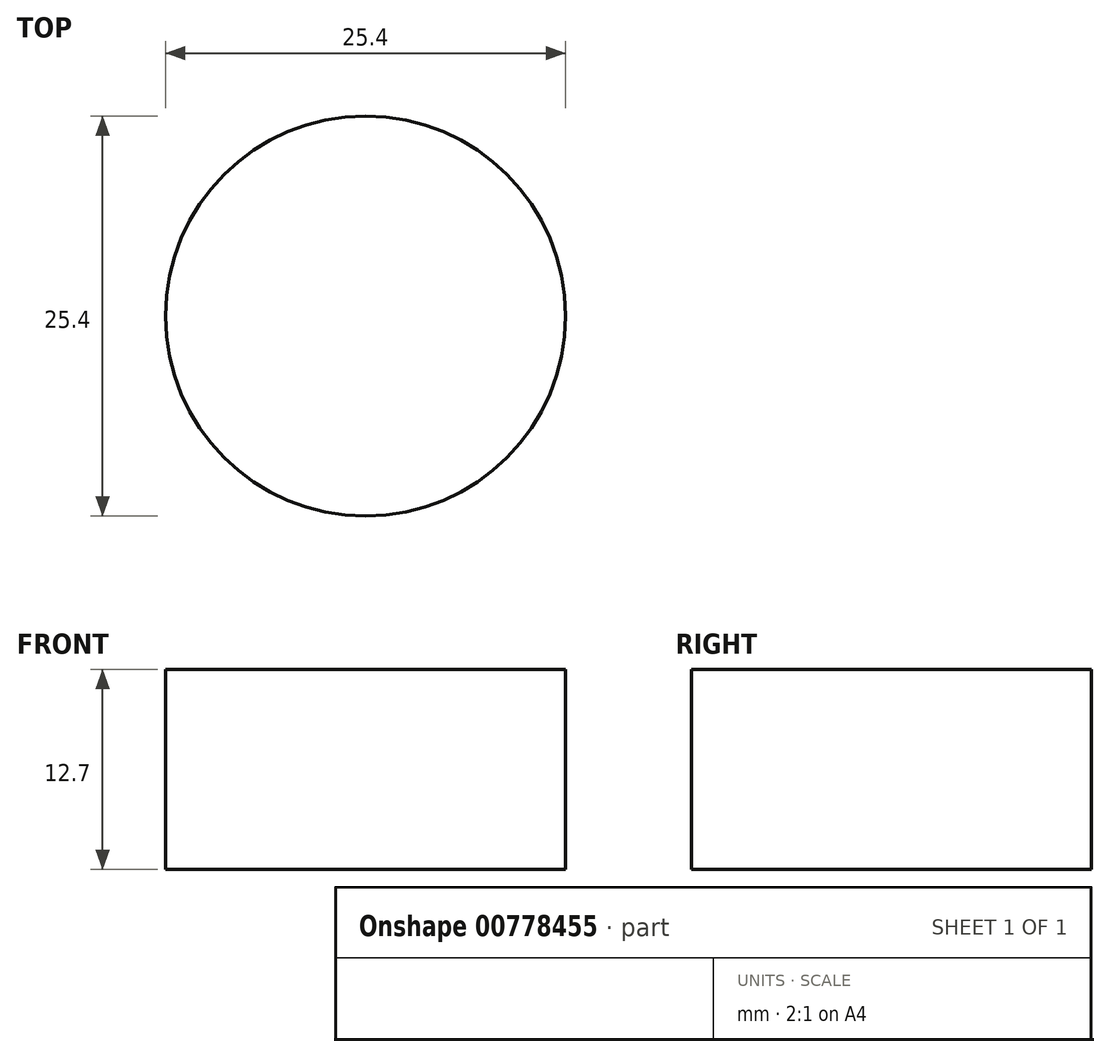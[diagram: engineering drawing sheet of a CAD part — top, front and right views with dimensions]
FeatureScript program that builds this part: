
annotation { "Feature Type Name" : "Feature", "Feature Type Description" : "" }
export const myFeature = defineFeature(function(context is Context, id is Id, definition is map)
    precondition{}
    {
        {
            var Q0;
            Q0=qCreatedBy(makeId("Top.planeOp"),FACE);
            var sketch = newSketch(context, id + "F0", { "sketchPlane" : qUnion([Q0])});
            skCircle(sketch, "E0", {"center": v(0, -2.32) * mm, "radius": 12.7 * mm});
            skSolve(sketch);
        }
        {
            var Q0;
            Q0 = qSketchRegion(id + "F0", true);
            extrude(context, id + "F1", {"entities" : qUnion([Q0]), "depth" : 12.7 * mm, "offsetDistance" : 25.4 * mm});
        }
    });
